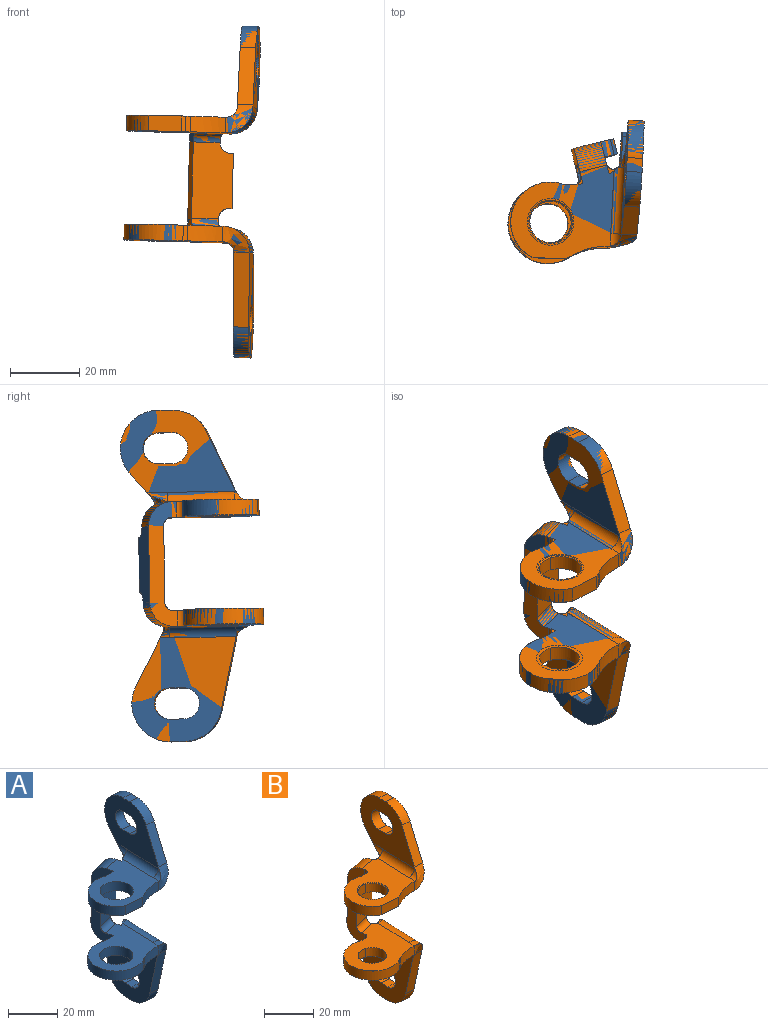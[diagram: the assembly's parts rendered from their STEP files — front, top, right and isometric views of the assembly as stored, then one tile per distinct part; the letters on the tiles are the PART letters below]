
ASSEMBLY  parts=2 mates=1
PART A: 72 faces, bbox 39.5x41.6x96 mm
  f0: plane 29.89x27.08mm, normal (0.02,0.02,1), area 449.5mm2, adj f18,f19,f20,f21,f22,f23,f24,f25
  f1: plane 29.82x27.08mm, normal (-0.02,-0.02,-1), area 449.5mm2, adj f16,f17,f18,f19,f20,f23,f24,f25
  f2: plane 5.57x5.12mm, normal (0.02,0.74,-0.67), area 33mm2, adj f3,f11,f13,f15
  f3: cylinder r=11mm len=18.43mm, axis (1,-0.05,-0.02), area 113.1mm2, adj f2,f4,f13,f15
  f4: plane 4.7x4.23mm, normal (0.02,0.02,1), area 18mm2, adj f3,f5,f13,f15
  f5: cylinder r=11mm len=10.29mm, axis (1,-0.05,-0.02), area 56.2mm2, adj f4,f13,f14,f15
  f6: plane 4.7x4.23mm, normal (-0.02,-0.02,-1), area 18mm2, adj f7,f9,f13,f15
  f7: cylinder r=4.5mm len=9.1mm, axis (1,-0.05,-0.02), area 63.6mm2, adj f6,f8,f13,f15
  f8: plane 4.7x4.23mm, normal (0.02,0.02,1), area 18mm2, adj f7,f9,f13,f15
  f9: cylinder r=4.5mm len=9.1mm, axis (1,-0.05,-0.02), area 63.6mm2, adj f6,f8,f13,f15
  f10: cylinder r=7.5mm len=7.38mm, axis (0.05,1,-0.02), area 32.2mm2, adj f11,f13,f17
  f11: bspline ~8.15x7.83mm, area 39.5mm2, adj f2,f10,f12,f20
  f12: cylinder r=3mm len=6.06mm, axis (0.05,1,-0.02), area 10.9mm2, adj f11,f15,f21
  f13: plane 33.34x23.93mm, normal (1,-0.05,-0.02), area 485.7mm2, adj f2,f3,f4,f5,f6,f7,f8,f9
  f14: plane 16.57x8.21mm, normal (-0.04,-0.9,0.44), area 82.4mm2, adj f5,f13,f15,f23
  f15: plane 33.45x23.95mm, normal (-1,0.05,0.02), area 485.7mm2, adj f2,f3,f4,f5,f6,f7,f8,f9
  f16: cylinder r=7.5mm len=7.85mm, axis (-0.05,-1,0.02), area 28.2mm2, adj f1,f13,f17,f23
  f17: cylinder r=7.5mm len=19.48mm, axis (-0.05,-1,0.02), area 225.8mm2, adj f1,f10,f13,f16,f20
  f18: cylinder r=11.5mm len=21.87mm, axis (0.02,0.02,1), area 153.4mm2, adj f0,f1,f19,f27
  f19: cylinder r=6mm len=4.52mm, axis (0.02,0.02,1), area 5.1mm2, adj f0,f1,f18,f47
  f20: cylinder r=20mm len=4.78mm, axis (0.02,0.02,1), area 14.3mm2, adj f0,f1,f11,f17,f21,f28
  f21: cylinder r=3mm len=19.3mm, axis (0.05,1,-0.02), area 90mm2, adj f0,f12,f15,f20,f22
  f22: cylinder r=3mm len=3.74mm, axis (-0.05,-1,0.02), area 10.8mm2, adj f0,f15,f21,f23
  f23: bspline ~9.28x9.03mm, area 45mm2, adj f0,f1,f13,f14,f15,f16,f22,f24
  f24: cylinder r=19mm len=10.23mm, axis (0.02,0.02,1), area 47.4mm2, adj f0,f1,f23,f25
  f25: plane 4.54x1.46mm, normal (0.48,-0.88,0), area 6.9mm2, adj f0,f1,f24,f26
  f26: cylinder r=11.5mm len=4.54mm, axis (0.02,0.02,1), area 6.1mm2, adj f0,f1,f25,f27
  f27: plane 9.5x4.71mm, normal (-0.04,-1,0.02), area 42.3mm2, adj f0,f1,f18,f26
  f28: plane 9.38x7.09mm, normal (0.97,0.24,-0.03), area 45.6mm2, adj f0,f1,f20,f29,f46,f48
  f29: cylinder r=3mm len=5.05mm, axis (-0.24,0.97,-0.01), area 21.2mm2, adj f28,f30,f45,f49
  f30: plane 4.61x2.05mm, normal (0.02,0.02,1), area 4.5mm2, adj f29,f31,f45,f49
  f31: plane 16.04x4.61mm, normal (0.97,0.24,-0.03), area 72mm2, adj f30,f32,f45,f49
  f32: plane 4.61x2.05mm, normal (-0.02,-0.02,-1), area 4.5mm2, adj f31,f45,f49,f51
  f33: plane 30.35x30.17mm, normal (1,-0.05,-0.02), area 603.6mm2, adj f34,f35,f36,f37,f38,f39,f40,f41
  f34: cylinder r=7.5mm len=7.62mm, axis (-0.05,-1,0.02), area 15.1mm2, adj f33,f52,f53
  f35: cylinder r=11mm len=10.83mm, axis (1,-0.05,-0.02), area 67.1mm2, adj f33,f36,f43,f55
  f36: plane 4.7x4.23mm, normal (-0.02,-0.02,-1), area 18mm2, adj f33,f35,f37,f55
  f37: cylinder r=11mm len=16.01mm, axis (1,-0.05,-0.02), area 101.5mm2, adj f33,f36,f38,f55
  f38: plane 14.15x7.25mm, normal (0.06,0.89,0.45), area 70.6mm2, adj f33,f37,f52,f55
  f39: plane 4.7x4.23mm, normal (0.02,0.02,1), area 18mm2, adj f33,f40,f42,f55
  f40: cylinder r=4.5mm len=9.1mm, axis (1,-0.05,-0.02), area 63.6mm2, adj f33,f39,f41,f55
  f41: plane 4.7x4.23mm, normal (-0.02,-0.02,-1), area 18mm2, adj f33,f40,f42,f55
  f42: cylinder r=4.5mm len=9.1mm, axis (1,-0.05,-0.02), area 63.6mm2, adj f33,f39,f41,f55
  f43: plane 21.53x4.75mm, normal (-0.06,-0.98,-0.2), area 98.4mm2, adj f33,f35,f55,f58
  f44: cylinder r=7.5mm len=7.73mm, axis (0.05,1,-0.02), area 21.1mm2, adj f53,f54,f58
  f45: plane 22.2x12.09mm, normal (0.24,-0.97,0.01), area 243.9mm2, adj f29,f30,f31,f32,f46,f50,f51,f64
  f46: cylinder r=2.5mm len=8.42mm, axis (-0.97,-0.24,0.03), area 31.4mm2, adj f1,f28,f45,f64
  f47: cylinder r=20mm len=5.11mm, axis (0.02,0.02,1), area 22.6mm2, adj f0,f1,f19,f64
  f48: cylinder r=7mm len=9.61mm, axis (0.97,0.24,-0.03), area 88mm2, adj f0,f28,f49,f64
  f49: plane 22.2x12.09mm, normal (-0.24,0.97,-0.01), area 243.9mm2, adj f29,f30,f31,f32,f48,f51,f64,f65
  f50: cylinder r=2.5mm len=8.31mm, axis (0.97,0.24,-0.03), area 31.4mm2, adj f45,f54,f64,f66
  f51: cylinder r=3mm len=5.13mm, axis (0.24,-0.97,0.01), area 21.2mm2, adj f32,f45,f49,f66
  f52: bspline ~8.57x7.43mm, area 32.6mm2, adj f34,f38,f56,f67
  f53: cylinder r=7.5mm len=19.69mm, axis (-0.05,-1,0.02), area 225.7mm2, adj f33,f34,f44,f54,f67
  f54: plane 29.82x27.93mm, normal (0.02,0.02,1), area 455.9mm2, adj f44,f50,f53,f58,f59,f60,f61,f62
  f55: plane 30.34x30.17mm, normal (-1,0.05,0.02), area 603.6mm2, adj f35,f36,f37,f38,f39,f40,f41,f42
  f56: cylinder r=3mm len=2.96mm, axis (-0.05,-1,0.02), area 5.1mm2, adj f52,f55,f68
  f57: cylinder r=3mm len=3.89mm, axis (0.05,1,-0.02), area 8.5mm2, adj f58,f68,f69
  f58: bspline ~8.54x8.45mm, area 41.9mm2, adj f43,f44,f54,f57,f59,f69
  f59: cylinder r=19mm len=10.23mm, axis (0.02,0.02,1), area 47.4mm2, adj f54,f58,f60,f69
  f60: plane 4.54x1.46mm, normal (0.48,-0.88,0), area 6.9mm2, adj f54,f59,f61,f69
  f61: cylinder r=11.5mm len=23.07mm, axis (0.02,0.02,1), area 203.2mm2, adj f54,f60,f62,f69
  f62: cylinder r=6mm len=4.52mm, axis (0.02,0.02,1), area 5.1mm2, adj f54,f61,f63,f69
  f63: cylinder r=20mm len=5.11mm, axis (0.02,0.02,1), area 22.6mm2, adj f54,f62,f64,f69
  f64: plane 36.03x10.77mm, normal (-0.97,-0.24,0.03), area 198.6mm2, adj f0,f1,f45,f46,f47,f48,f49,f50
  f65: cylinder r=7mm len=9.29mm, axis (-0.97,-0.24,0.03), area 88mm2, adj f49,f64,f66,f69
  f66: plane 9.49x6.98mm, normal (0.97,0.24,-0.03), area 45.6mm2, adj f50,f51,f54,f65,f67,f69
  f67: cylinder r=20mm len=4.78mm, axis (0.02,0.02,1), area 14.3mm2, adj f52,f53,f54,f66,f68,f69
  f68: cylinder r=3mm len=19.39mm, axis (-0.05,-1,0.02), area 89.9mm2, adj f55,f56,f57,f67,f69
  f69: plane 29.87x27.98mm, normal (-0.02,-0.02,-1), area 455.9mm2, adj f57,f58,f59,f60,f61,f62,f63,f64
  f70: cylinder r=6.73mm len=13.56mm, axis (0.02,0.02,1), area 190.3mm2, adj f54,f69
  f71: cylinder r=6.73mm len=13.56mm, axis (0.02,0.02,1), area 190.3mm2, adj f0,f1
PART B: 82 faces, bbox 39.5x41.6x96 mm
  f0: cylinder r=11mm len=18.43mm, axis (1,-0.05,-0.02), area 113.1mm2, adj f1,f7,f10,f12
  f1: plane 4.7x4.23mm, normal (0.02,0.02,1), area 18mm2, adj f0,f2,f10,f12
  f2: cylinder r=11mm len=10.29mm, axis (1,-0.05,-0.02), area 56.2mm2, adj f1,f9,f10,f12
  f3: cylinder r=4.5mm len=9.1mm, axis (1,-0.05,-0.02), area 63.6mm2, adj f4,f6,f10,f12
  f4: plane 4.7x4.23mm, normal (-0.02,-0.02,-1), area 18mm2, adj f3,f5,f10,f12
  f5: cylinder r=4.5mm len=9.1mm, axis (1,-0.05,-0.02), area 63.6mm2, adj f4,f6,f10,f12
  f6: plane 4.7x4.23mm, normal (0.02,0.02,1), area 18mm2, adj f3,f5,f10,f12
  f7: plane 5.57x5.12mm, normal (0.02,0.74,-0.67), area 33mm2, adj f0,f10,f12,f13
  f8: cylinder r=3mm len=6.06mm, axis (0.05,1,-0.02), area 10.9mm2, adj f10,f13,f14
  f9: plane 16.57x8.21mm, normal (-0.04,-0.9,0.44), area 82.4mm2, adj f2,f10,f12,f21
  f10: plane 33.45x23.95mm, normal (-1,0.05,0.02), area 485.7mm2, adj f0,f1,f2,f3,f4,f5,f6,f7
  f11: cylinder r=7.5mm len=7.38mm, axis (0.05,1,-0.02), area 32.2mm2, adj f12,f13,f23
  f12: plane 33.34x23.93mm, normal (1,-0.05,-0.02), area 485.7mm2, adj f0,f1,f2,f3,f4,f5,f6,f7
  f13: bspline ~8.15x7.83mm, area 39.5mm2, adj f7,f8,f11,f31
  f14: cylinder r=3mm len=19.3mm, axis (0.05,1,-0.02), area 90.2mm2, adj f8,f10,f15,f31,f50
  f15: cylinder r=3mm len=3.74mm, axis (-0.05,-1,0.02), area 10.8mm2, adj f10,f14,f21,f50
  f16: cone r=6mm half-angle=45deg, axis (0.02,0.02,1), area 8.2mm2, adj f17,f29,f50
  f17: cone r=6mm half-angle=45deg, axis (0.02,0.02,1), area 8.2mm2, adj f16,f30,f50
  f18: cylinder r=11.5mm len=4.54mm, axis (0.02,0.02,1), area 6.1mm2, adj f19,f28,f50,f52
  f19: plane 4.54x1.46mm, normal (0.48,-0.88,0), area 6.9mm2, adj f18,f20,f50,f52
  f20: cylinder r=19mm len=10.23mm, axis (0.02,0.02,1), area 47.4mm2, adj f19,f21,f50,f52
  f21: bspline ~9.28x9.03mm, area 45mm2, adj f9,f10,f12,f15,f20,f22,f50,f52
  f22: cylinder r=7.5mm len=7.85mm, axis (-0.05,-1,0.02), area 28.2mm2, adj f12,f21,f23,f52
  f23: cylinder r=7.5mm len=19.48mm, axis (0.05,1,-0.02), area 226mm2, adj f11,f12,f22,f31,f52
  f24: cylinder r=20mm len=4.56mm, axis (0.02,0.02,1), area 11.6mm2, adj f25,f50,f51,f52
  f25: cylinder r=6mm len=4.52mm, axis (0.02,0.02,1), area 5.1mm2, adj f24,f27,f50,f52
  f26: cylinder r=3.51mm len=5.33mm, axis (-0.64,0.77,0), area 2.1mm2, adj f27,f52
  f27: cylinder r=11.5mm len=21.87mm, axis (0.02,0.02,1), area 153.4mm2, adj f25,f26,f28,f50,f52
  f28: plane 9.5x4.71mm, normal (-0.04,-1,0.02), area 42.3mm2, adj f18,f27,f50,f52
  f29: cylinder r=6mm len=11.79mm, axis (0.02,0.02,1), area 79.2mm2, adj f16,f30,f52
  f30: cylinder r=6mm len=11.79mm, axis (0.02,0.02,1), area 79.2mm2, adj f17,f29,f52
  f31: cylinder r=2mm len=4.77mm, axis (0.02,0.02,1), area 18.5mm2, adj f13,f14,f23,f32,f49,f50,f52,f53
  f32: plane 7.05x6.47mm, normal (0.97,0.24,-0.03), area 32.1mm2, adj f31,f33,f49,f53
  f33: cylinder r=3mm len=5.05mm, axis (-0.24,0.97,-0.01), area 21.2mm2, adj f32,f34,f54,f55
  f34: plane 4.61x2.05mm, normal (0.02,0.02,1), area 4.5mm2, adj f33,f35,f54,f55
  f35: plane 16.03x4.61mm, normal (0.97,0.24,-0.03), area 72mm2, adj f34,f36,f54,f55
  f36: plane 4.61x2.05mm, normal (-0.02,-0.02,-1), area 4.5mm2, adj f35,f37,f54,f55
  f37: cylinder r=3mm len=5.13mm, axis (0.24,-0.97,0.01), area 21.2mm2, adj f36,f54,f55,f56
  f38: cylinder r=11mm len=10.83mm, axis (1,-0.05,-0.02), area 67.1mm2, adj f39,f46,f48,f58
  f39: plane 4.7x4.23mm, normal (-0.02,-0.02,-1), area 18mm2, adj f38,f40,f46,f58
  f40: cylinder r=11mm len=16.01mm, axis (1,-0.05,-0.02), area 101.5mm2, adj f39,f41,f46,f58
  f41: plane 14.15x7.25mm, normal (0.06,0.89,0.45), area 70.6mm2, adj f40,f46,f57,f58
  f42: plane 4.7x4.23mm, normal (0.02,0.02,1), area 18mm2, adj f43,f45,f46,f58
  f43: cylinder r=4.5mm len=9.1mm, axis (1,-0.05,-0.02), area 63.6mm2, adj f42,f44,f46,f58
  f44: plane 4.7x4.23mm, normal (-0.02,-0.02,-1), area 18mm2, adj f43,f45,f46,f58
  f45: cylinder r=4.5mm len=9.1mm, axis (1,-0.05,-0.02), area 63.6mm2, adj f42,f44,f46,f58
  f46: plane 30.35x30.17mm, normal (1,-0.05,-0.02), area 603.6mm2, adj f38,f39,f40,f41,f42,f43,f44,f45
  f47: cylinder r=7.5mm len=7.62mm, axis (-0.05,-1,0.02), area 15.1mm2, adj f46,f57,f61
  f48: plane 21.53x4.75mm, normal (-0.06,-0.98,-0.2), area 98.4mm2, adj f38,f46,f58,f65
  f49: cylinder r=7mm len=9.64mm, axis (0.97,0.24,-0.03), area 88mm2, adj f31,f32,f50,f55,f72
  f50: plane 29.92x27.08mm, normal (0.02,0.02,1), area 470.4mm2, adj f14,f15,f16,f17,f18,f19,f20,f21
  f51: cylinder r=2mm len=4.58mm, axis (-0.02,-0.02,-1), area 16mm2, adj f24,f50,f52,f72
  f52: plane 29.84x27.08mm, normal (-0.02,-0.02,-1), area 479.9mm2, adj f18,f19,f20,f21,f22,f23,f24,f25
  f53: cylinder r=2.5mm len=8.45mm, axis (-0.97,-0.24,0.03), area 31.4mm2, adj f31,f32,f52,f54,f72
  f54: plane 22.2x12.09mm, normal (0.24,-0.97,0.01), area 243.9mm2, adj f33,f34,f35,f36,f37,f53,f62,f72
  f55: plane 22.2x12.09mm, normal (-0.24,0.97,-0.01), area 243.9mm2, adj f33,f34,f35,f36,f37,f49,f72,f73
  f56: plane 6.97x6.58mm, normal (0.97,0.24,-0.03), area 32.1mm2, adj f37,f62,f73,f74
  f57: bspline ~8.57x7.43mm, area 32.6mm2, adj f41,f47,f59,f74
  f58: plane 30.34x30.17mm, normal (-1,0.05,0.02), area 603.6mm2, adj f38,f39,f40,f41,f42,f43,f44,f45
  f59: cylinder r=3mm len=2.96mm, axis (-0.05,-1,0.02), area 5.1mm2, adj f57,f58,f75
  f60: cylinder r=7.5mm len=7.73mm, axis (0.05,1,-0.02), area 21.1mm2, adj f61,f65,f76
  f61: cylinder r=7.5mm len=19.69mm, axis (-0.05,-1,0.02), area 225.9mm2, adj f46,f47,f60,f74,f76
  f62: cylinder r=2.5mm len=8.34mm, axis (0.97,0.24,-0.03), area 31.4mm2, adj f54,f56,f72,f74,f76
  f63: cylinder r=3.53mm len=5.32mm, axis (-0.64,0.77,0), area 2.1mm2, adj f68,f76
  f64: cylinder r=3mm len=3.89mm, axis (0.05,1,-0.02), area 8.5mm2, adj f65,f75,f78
  f65: bspline ~8.54x8.45mm, area 41.9mm2, adj f48,f60,f64,f66,f76,f78
  f66: cylinder r=19mm len=10.23mm, axis (0.02,0.02,1), area 47.4mm2, adj f65,f67,f76,f78
  f67: plane 4.54x1.46mm, normal (0.48,-0.88,0), area 6.9mm2, adj f66,f68,f76,f78
  f68: cylinder r=11.5mm len=23.07mm, axis (0.02,0.02,1), area 203.2mm2, adj f63,f67,f69,f76,f78
  f69: cylinder r=6mm len=4.52mm, axis (0.02,0.02,1), area 5.1mm2, adj f68,f70,f76,f78
  f70: cylinder r=20mm len=4.56mm, axis (0.02,0.02,1), area 11.6mm2, adj f69,f71,f76,f78
  f71: cylinder r=2mm len=4.58mm, axis (-0.02,-0.02,-1), area 16mm2, adj f70,f72,f76,f78
  f72: plane 36.01x8.52mm, normal (-0.97,-0.24,0.03), area 177.8mm2, adj f49,f50,f51,f52,f53,f54,f55,f62
  f73: cylinder r=7mm len=9.32mm, axis (-0.97,-0.24,0.03), area 88mm2, adj f55,f56,f72,f74,f78
  f74: cylinder r=2mm len=4.77mm, axis (0.02,0.02,1), area 18.5mm2, adj f56,f57,f61,f62,f73,f75,f76,f78
  f75: cylinder r=3mm len=19.39mm, axis (-0.05,-1,0.02), area 90.1mm2, adj f58,f59,f64,f74,f78
  f76: plane 29.84x27.94mm, normal (0.02,0.02,1), area 495.5mm2, adj f60,f61,f62,f63,f65,f66,f67,f68
  f77: cylinder r=5.75mm len=11.3mm, axis (0.02,0.02,1), area 75.9mm2, adj f76,f79,f80
  f78: plane 29.89x27.99mm, normal (-0.02,-0.02,-1), area 486.4mm2, adj f64,f65,f66,f67,f68,f69,f70,f71
  f79: cone r=5.75mm half-angle=45deg, axis (-0.02,-0.02,-1), area 7.9mm2, adj f77,f78,f81
  f80: cylinder r=5.75mm len=11.3mm, axis (0.02,0.02,1), area 75.9mm2, adj f76,f77,f81
  f81: cone r=5.75mm half-angle=45deg, axis (-0.02,-0.02,-1), area 7.9mm2, adj f78,f79,f80
PLACE A rot(axis=(1,0.01,-0.02),0deg) t=(-1516.76,675.31,-323.3)mm
PLACE B t=(-1523.95,670.64,-630.28)mm
MATE fastened A.f5 <-> B.f3  axis (1,-0.05,-0.02) through (-111.18,-107.44,-19.89)mm
